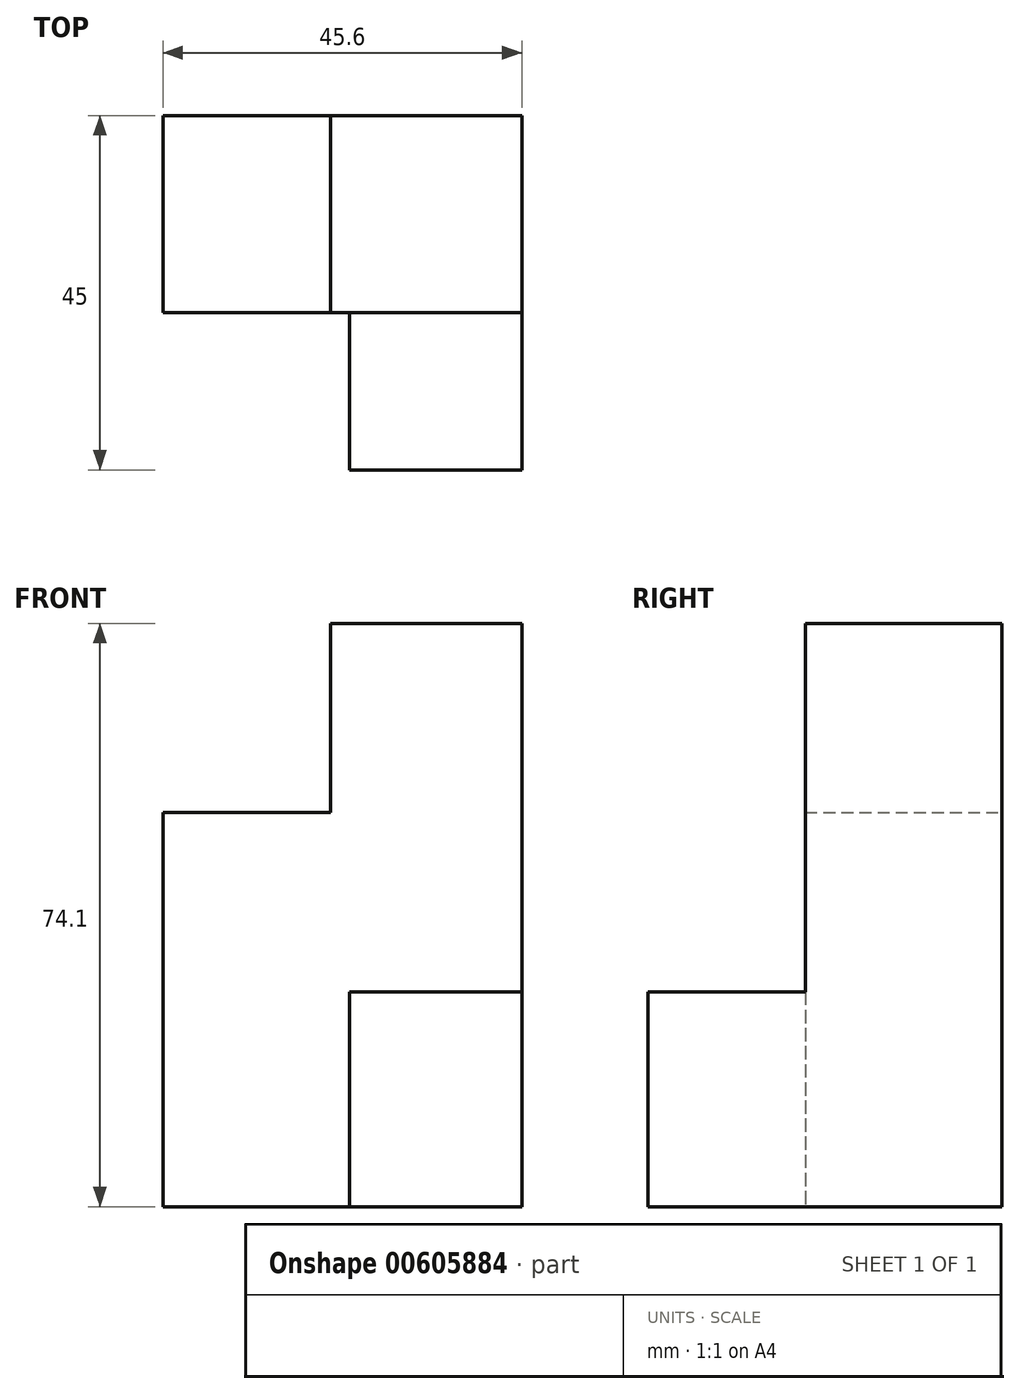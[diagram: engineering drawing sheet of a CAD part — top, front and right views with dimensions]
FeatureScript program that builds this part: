
annotation { "Feature Type Name" : "Feature", "Feature Type Description" : "" }
export const myFeature = defineFeature(function(context is Context, id is Id, definition is map)
    precondition{}
    {
        {
            var Q0;
            Q0=qCreatedBy(makeId("Front.planeOp"),FACE);
            var sketch = newSketch(context, id + "F0", { "sketchPlane" : qUnion([Q0])});
            skLineSegment(sketch, "E0", {"start": v(-5.85, 40.2) * mm, "end": v(-30.15, 40.2) * mm});
            skLineSegment(sketch, "E1", {"start": v(-30.15, 40.2) * mm, "end": v(-30.15, 16.2) * mm});
            skLineSegment(sketch, "E2", {"start": v(-5.85, 40.2) * mm, "end": v(-5.85, 16.2) * mm});
            skLineSegment(sketch, "E3", {"start": v(-5.85, 16.2) * mm, "end": v(-30.15, 16.2) * mm});
            skLineSegment(sketch, "E4", {"start": v(-5.85, 16.2) * mm, "end": v(-5.85, -8.4) * mm});
            skLineSegment(sketch, "E5", {"start": v(-5.85, -8.4) * mm, "end": v(-30.15, -8.4) * mm});
            skLineSegment(sketch, "E6", {"start": v(-30.15, 16.2) * mm, "end": v(-30.15, -8.4) * mm});
            skLineSegment(sketch, "E7", {"start": v(-5.85, -8.4) * mm, "end": v(-5.85, -33.9) * mm});
            skLineSegment(sketch, "E8", {"start": v(-5.85, -33.9) * mm, "end": v(-30.15, -33.9) * mm});
            skLineSegment(sketch, "E9", {"start": v(-30.15, -33.9) * mm, "end": v(-30.15, -8.4) * mm});
            skLineSegment(sketch, "E10", {"start": v(-30.15, 16.2) * mm, "end": v(-51.45, 16.2) * mm});
            skLineSegment(sketch, "E11", {"start": v(-51.45, 16.2) * mm, "end": v(-51.45, -8.4) * mm});
            skLineSegment(sketch, "E12", {"start": v(-30.15, -8.4) * mm, "end": v(-51.45, -8.4) * mm});
            skLineSegment(sketch, "E13", {"start": v(-30.15, -33.9) * mm, "end": v(-51.45, -33.9) * mm});
            skLineSegment(sketch, "E14", {"start": v(-51.45, -33.9) * mm, "end": v(-51.45, -8.4) * mm});
            skSolve(sketch);
        }
        {
            var Q0;
            Q0 = qSketchRegion(id + "F0", true);
            extrude(context, id + "F1", {"entities" : qUnion([Q0]), "depth" : 25 * mm, "offsetDistance" : 25 * mm});
        }
        {
            var Q0;
            Q0=makeQuery(id+"F1.opExtrude","CAP_FACE",FACE,{"disambiguationData":[OSD([sQuery(id+"F0.wireOp",EDGE,"E0"),sQuery(id+"F0.wireOp",EDGE,"E1"),sQuery(id+"F0.wireOp",EDGE,"E2"),sQuery(id+"F0.wireOp",EDGE,"E4"),sQuery(id+"F0.wireOp",EDGE,"E7"),sQuery(id+"F0.wireOp",EDGE,"E8"),sQuery(id+"F0.wireOp",EDGE,"E10"),sQuery(id+"F0.wireOp",EDGE,"E11"),sQuery(id+"F0.wireOp",EDGE,"E13"),sQuery(id+"F0.wireOp",EDGE,"E14")])],"isStart":false});
            var sketch = newSketch(context, id + "F2", { "sketchPlane" : qUnion([Q0])});
            skLineSegment(sketch, "E15", {"start": v(-5.85, -6.6) * mm, "end": v(-27.75, -6.6) * mm});
            skLineSegment(sketch, "E16", {"start": v(-27.75, -6.6) * mm, "end": v(-27.75, -33.9) * mm});
            skLineSegment(sketch, "E17", {"start": v(-27.75, -33.9) * mm, "end": v(-5.85, -33.9) * mm});
            skLineSegment(sketch, "E18", {"start": v(-5.85, -33.9) * mm, "end": v(-5.85, -6.6) * mm});
            skSolve(sketch);
        }
        {
            var Q0;
            Q0 = qSketchRegion(id + "F2", true);
            extrude(context, id + "F3", {"entities" : qUnion([Q0]), "operationType" : NewBodyOperationType.ADD, "depth" : 20 * mm, "offsetDistance" : 25 * mm});
        }
    });
